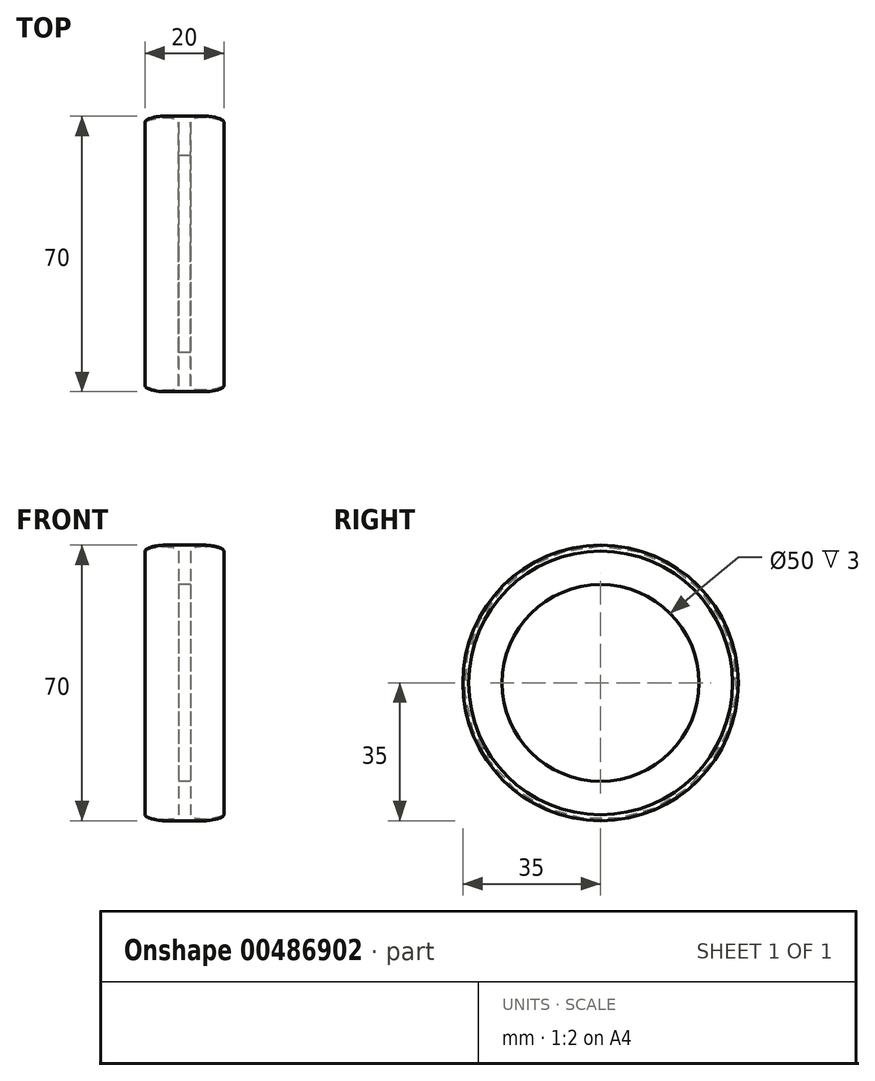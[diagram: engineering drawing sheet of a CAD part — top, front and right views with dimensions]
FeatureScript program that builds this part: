
annotation { "Feature Type Name" : "Feature", "Feature Type Description" : "" }
export const myFeature = defineFeature(function(context is Context, id is Id, definition is map)
    precondition{}
    {
        {
            var Q0;
            Q0=qCreatedBy(makeId("Front.planeOp"),FACE);
            var sketch = newSketch(context, id + "F0", { "sketchPlane" : qUnion([Q0])});
            skLineSegment(sketch, "E0", {"start": v(-10, 0) * mm, "end": v(10, 0) * mm, "construction": true});
            skLineSegment(sketch, "E1.bottom", {"start": v(-5, 35) * mm, "end": v(5, 35) * mm});
            skLineSegment(sketch, "E1.top", {"start": v(-10, 33.5) * mm, "end": v(10, 33.5) * mm, "construction": true});
            skLineSegment(sketch, "E1.left", {"start": v(-10, 35) * mm, "end": v(-10, 33.5) * mm, "construction": true});
            skLineSegment(sketch, "E1.right", {"start": v(10, 35) * mm, "end": v(10, 33.5) * mm, "construction": true});
            skLineSegment(sketch, "E2", {"start": v(-5, 35) * mm, "end": v(5, 35) * mm, "construction": true});
            skFitSpline(sketch, "E3", {"points": [v(-10, 33.5) * mm, v(-5, 35) * mm], "startDerivative": vector(0, 2.25) * mm, "endDerivative": vector(7.5, 0) * mm});
            skLineSegment(sketch, "E4", {"start": v(-5, 35) * mm, "end": v(-10, 35) * mm, "construction": true});
            skLineSegment(sketch, "E5", {"start": v(5, 35) * mm, "end": v(10, 35) * mm, "construction": true});
            skFitSpline(sketch, "E6", {"points": [v(5, 35) * mm, v(10, 33.5) * mm], "startDerivative": vector(7.5, 0) * mm, "endDerivative": vector(0, -2.25) * mm});
            skLineSegment(sketch, "E7.top", {"start": v(-1.5, 25) * mm, "end": v(0, 25) * mm});
            skLineSegment(sketch, "E7.left", {"start": v(-1.5, 33.5) * mm, "end": v(-1.5, 25) * mm});
            skFitSpline(sketch, "E8", {"points": [v(-10, 33.5) * mm, v(-1.5, 33.5) * mm], "startDerivative": vector(7.5, 4.5) * mm, "endDerivative": vector(0, -4.5) * mm});
            skLineSegment(sketch, "E9", {"start": v(0, 0) * mm, "end": v(0, 38.7) * mm, "construction": true});
            skFitSpline(sketch, "E10.MirrorCS", {"points": [v(10, 33.5) * mm, v(1.5, 33.5) * mm], "startDerivative": vector(-7.5, 4.5) * mm, "endDerivative": vector(0, -4.5) * mm});
            skLineSegment(sketch, "E11.MirrorCS", {"start": v(1.5, 33.5) * mm, "end": v(1.5, 25) * mm});
            skLineSegment(sketch, "E12.MirrorCS", {"start": v(1.5, 25) * mm, "end": v(0, 25) * mm});
            skSolve(sketch);
        }
        {
            var Q0;
            Q0=makeQuery(id+"F0.imprint","IMPRINT",FACE,{"disambiguationData":[TD([[makeQuery(id+"F0.imprint","IMPRINT",EDGE,{"derivedFrom":sQuery(id+"F0.wireOp",EDGE,"E1.bottom")}),-1.0]])]});
            var Q1;
            Q1=sQuery(id+"F0.wireOp",EDGE,"E0");
            revolve(context, id + "F1", {"entities" : qUnion([Q0]), "axis" : qUnion([Q1]), "revolveType" : RevolveType.FULL});
        }
    });
